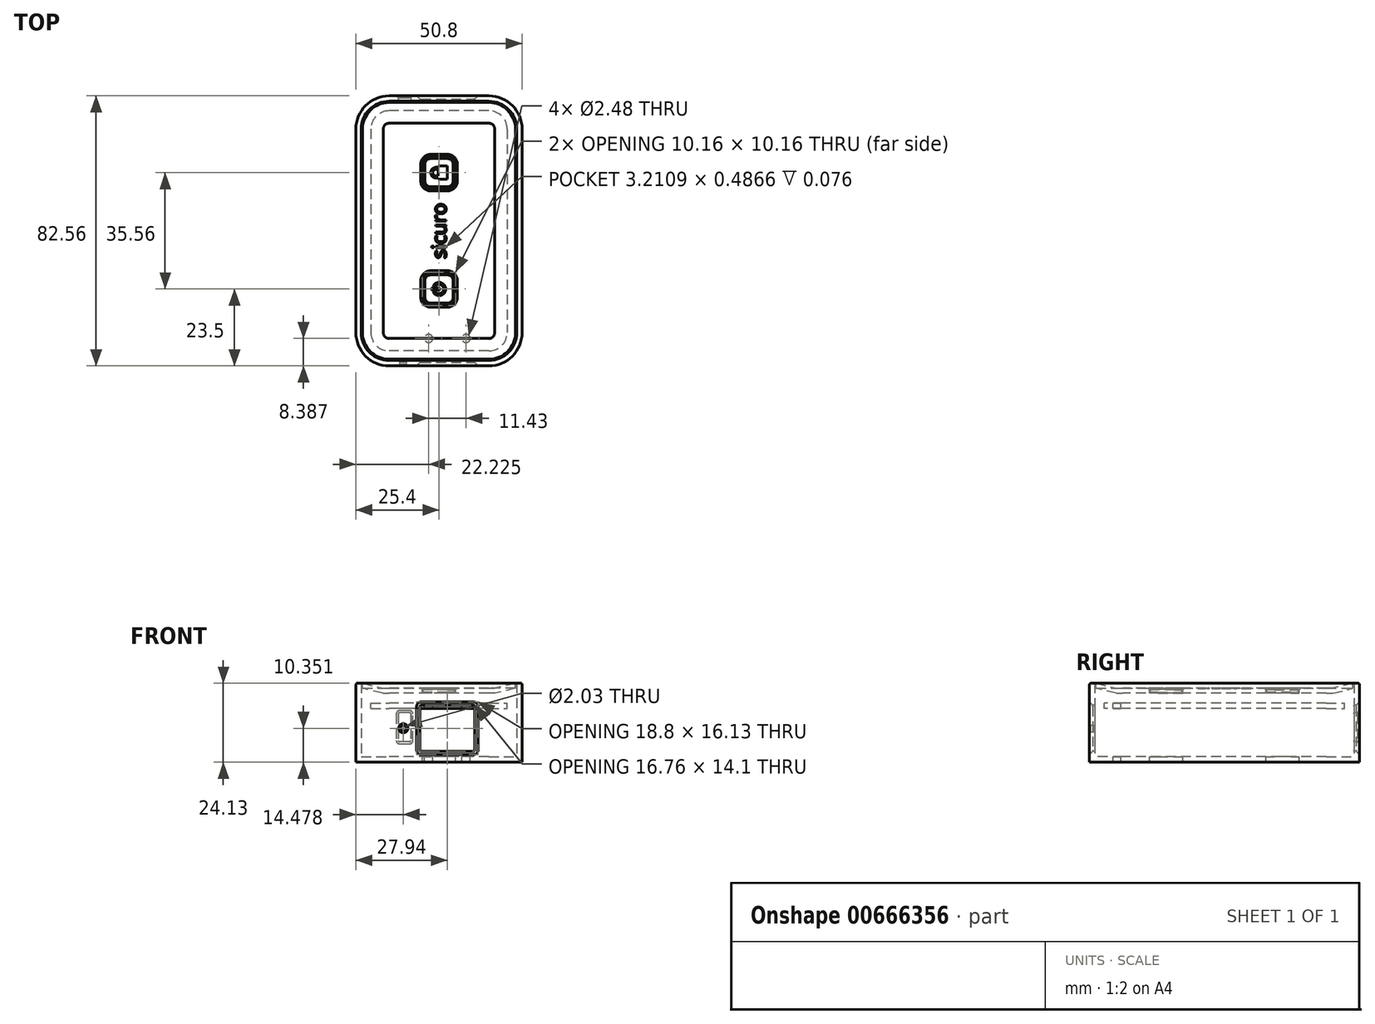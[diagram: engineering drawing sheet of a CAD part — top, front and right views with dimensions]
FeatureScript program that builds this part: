
annotation { "Feature Type Name" : "Feature", "Feature Type Description" : "" }
export const myFeature = defineFeature(function(context is Context, id is Id, definition is map)
    precondition{}
    {
        {
            var Q0;
            Q0=qCreatedBy(makeId("Top.planeOp"),FACE);
            var sketch = newSketch(context, id + "F0", { "sketchPlane" : qUnion([Q0])});
            skLineSegment(sketch, "E0.bottom", {"start": v(25.4, 41.28) * mm, "end": v(-25.4, 41.28) * mm});
            skLineSegment(sketch, "E0.top", {"start": v(25.4, -41.28) * mm, "end": v(-25.4, -41.28) * mm});
            skLineSegment(sketch, "E0.left", {"start": v(25.4, 41.28) * mm, "end": v(25.4, -41.28) * mm});
            skLineSegment(sketch, "E0.right", {"start": v(-25.4, 41.28) * mm, "end": v(-25.4, -41.28) * mm});
            skPoint(sketch, "E0.middle", {"position": v(0, 0) * mm});
            skSolve(sketch);
        }
        {
            var Q0;
            Q0 = qSketchRegion(id + "F0", true);
            extrude(context, id + "F1", {"entities" : qUnion([Q0]), "depth" : 24.13 * mm, "offsetDistance" : 25.4 * mm});
        }
        {
            var Q0;
            Q0=makeQuery(id+"F1.opExtrude","SWEPT_EDGE",EDGE,{"disambiguationData":[OSD([sQuery(id+"F0.wireOp",EDGE,"E0.top"),sQuery(id+"F0.wireOp",EDGE,"E0.left")])]});
            var Q1;
            Q1=makeQuery(id+"F1.opExtrude","SWEPT_EDGE",EDGE,{"disambiguationData":[OSD([sQuery(id+"F0.wireOp",EDGE,"E0.top"),sQuery(id+"F0.wireOp",EDGE,"E0.right")])]});
            var Q2;
            Q2=makeQuery(id+"F1.opExtrude","SWEPT_EDGE",EDGE,{"disambiguationData":[OSD([sQuery(id+"F0.wireOp",EDGE,"E0.bottom"),sQuery(id+"F0.wireOp",EDGE,"E0.left")])]});
            var Q3;
            Q3=makeQuery(id+"F1.opExtrude","SWEPT_EDGE",EDGE,{"disambiguationData":[OSD([sQuery(id+"F0.wireOp",EDGE,"E0.bottom"),sQuery(id+"F0.wireOp",EDGE,"E0.right")])]});
            fillet(context, id + "F2", {"entities" : qUnion([Q0, Q1, Q2, Q3]), "radius" : 10.16 * mm, "tangentPropagation" : true, "allowEdgeOverflow" : false});
        }
        {
            var Q0;
            Q0=makeQuery(id+"F1.opExtrude","CAP_FACE",FACE,{"disambiguationData":[OSD([sQuery(id+"F0.wireOp",EDGE,"E0.bottom"),sQuery(id+"F0.wireOp",EDGE,"E0.top"),sQuery(id+"F0.wireOp",EDGE,"E0.left"),sQuery(id+"F0.wireOp",EDGE,"E0.right")])],"isStart":false});
            shell(context, id + "F3", {"entities" : qUnion([Q0]), "thickness" : 1.65 * mm});
        }
        {
            var Q0;
            Q0=makeQuery(id+"F1.opExtrude","CAP_EDGE",EDGE,{"disambiguationData":[OSD([sQuery(id+"F0.wireOp",EDGE,"E0.right")])],"isStart":false});
            var Q1;
            {var subQ0=sQuery(id+"F0.wireOp",EDGE,"E0.right");var subQ1=sQuery(id+"F0.wireOp",EDGE,"E0.bottom");Q1=makeQuery(id+"F2.opFillet","BLEND_EDGE",EDGE,{"blendedFrom":[makeQuery(id+"F1.opExtrude","SWEPT_EDGE",EDGE,{"disambiguationData":[OSD([subQ1,subQ0])]}),makeQuery(id+"F1.opExtrude","CAP_FACE",FACE,{"disambiguationData":[OSD([subQ1,sQuery(id+"F0.wireOp",EDGE,"E0.top"),sQuery(id+"F0.wireOp",EDGE,"E0.left"),subQ0])],"isStart":false})],"blendedInto":[makeQuery(id+"F1.opExtrude","CAP_FACE",FACE,{"disambiguationData":[OSD([subQ1,sQuery(id+"F0.wireOp",EDGE,"E0.top"),sQuery(id+"F0.wireOp",EDGE,"E0.left"),subQ0])],"isStart":false})]});}
            var Q2;
            Q2=makeQuery(id+"F1.opExtrude","CAP_EDGE",EDGE,{"disambiguationData":[OSD([sQuery(id+"F0.wireOp",EDGE,"E0.bottom")])],"isStart":false});
            var Q3;
            {var subQ0=sQuery(id+"F0.wireOp",EDGE,"E0.left");var subQ1=sQuery(id+"F0.wireOp",EDGE,"E0.bottom");Q3=makeQuery(id+"F2.opFillet","BLEND_EDGE",EDGE,{"blendedFrom":[makeQuery(id+"F1.opExtrude","SWEPT_EDGE",EDGE,{"disambiguationData":[OSD([subQ1,subQ0])]}),makeQuery(id+"F1.opExtrude","CAP_FACE",FACE,{"disambiguationData":[OSD([subQ1,sQuery(id+"F0.wireOp",EDGE,"E0.top"),subQ0,sQuery(id+"F0.wireOp",EDGE,"E0.right")])],"isStart":false})],"blendedInto":[makeQuery(id+"F1.opExtrude","CAP_FACE",FACE,{"disambiguationData":[OSD([subQ1,sQuery(id+"F0.wireOp",EDGE,"E0.top"),subQ0,sQuery(id+"F0.wireOp",EDGE,"E0.right")])],"isStart":false})]});}
            var Q4;
            Q4=makeQuery(id+"F1.opExtrude","CAP_EDGE",EDGE,{"disambiguationData":[OSD([sQuery(id+"F0.wireOp",EDGE,"E0.left")])],"isStart":false});
            var Q5;
            {var subQ0=sQuery(id+"F0.wireOp",EDGE,"E0.left");var subQ1=sQuery(id+"F0.wireOp",EDGE,"E0.top");Q5=makeQuery(id+"F2.opFillet","BLEND_EDGE",EDGE,{"blendedFrom":[makeQuery(id+"F1.opExtrude","SWEPT_EDGE",EDGE,{"disambiguationData":[OSD([subQ1,subQ0])]}),makeQuery(id+"F1.opExtrude","CAP_FACE",FACE,{"disambiguationData":[OSD([sQuery(id+"F0.wireOp",EDGE,"E0.bottom"),subQ1,subQ0,sQuery(id+"F0.wireOp",EDGE,"E0.right")])],"isStart":false})],"blendedInto":[makeQuery(id+"F1.opExtrude","CAP_FACE",FACE,{"disambiguationData":[OSD([sQuery(id+"F0.wireOp",EDGE,"E0.bottom"),subQ1,subQ0,sQuery(id+"F0.wireOp",EDGE,"E0.right")])],"isStart":false})]});}
            var Q6;
            {var subQ0=sQuery(id+"F0.wireOp",EDGE,"E0.right");var subQ1=sQuery(id+"F0.wireOp",EDGE,"E0.top");Q6=makeQuery(id+"F2.opFillet","BLEND_EDGE",EDGE,{"blendedFrom":[makeQuery(id+"F1.opExtrude","SWEPT_EDGE",EDGE,{"disambiguationData":[OSD([subQ1,subQ0])]}),makeQuery(id+"F1.opExtrude","CAP_FACE",FACE,{"disambiguationData":[OSD([sQuery(id+"F0.wireOp",EDGE,"E0.bottom"),subQ1,sQuery(id+"F0.wireOp",EDGE,"E0.left"),subQ0])],"isStart":false})],"blendedInto":[makeQuery(id+"F1.opExtrude","CAP_FACE",FACE,{"disambiguationData":[OSD([sQuery(id+"F0.wireOp",EDGE,"E0.bottom"),subQ1,sQuery(id+"F0.wireOp",EDGE,"E0.left"),subQ0])],"isStart":false})]});}
            var Q7;
            Q7=makeQuery(id+"F1.opExtrude","CAP_EDGE",EDGE,{"disambiguationData":[OSD([sQuery(id+"F0.wireOp",EDGE,"E0.top")])],"isStart":false});
            fillet(context, id + "F4", {"entities" : qUnion([Q0, Q1, Q2, Q3, Q4, Q5, Q6, Q7]), "radius" : 0.5 * mm, "tangentPropagation" : true, "allowEdgeOverflow" : false});
        }
        {
            var Q0;
            Q0=makeQuery(id+"F1.opExtrude","CAP_FACE",FACE,{"disambiguationData":[OSD([sQuery(id+"F0.wireOp",EDGE,"E0.bottom"),sQuery(id+"F0.wireOp",EDGE,"E0.top"),sQuery(id+"F0.wireOp",EDGE,"E0.left"),sQuery(id+"F0.wireOp",EDGE,"E0.right")])],"isStart":false});
            var sketch = newSketch(context, id + "F5", { "sketchPlane" : qUnion([Q0])});
            skArc(sketch, "E1.0", {"start": v(-15.24, 39.24) * mm, "mid": v(-20.99, 36.86) * mm, "end": v(-23.37, 31.12) * mm});
            skLineSegment(sketch, "E1.1", {"start": v(15.24, 39.24) * mm, "end": v(-15.24, 39.24) * mm});
            skLineSegment(sketch, "E1.2", {"start": v(-23.37, 31.12) * mm, "end": v(-23.37, -31.12) * mm});
            skArc(sketch, "E1.3", {"start": v(23.37, 31.12) * mm, "mid": v(20.99, 36.86) * mm, "end": v(15.24, 39.24) * mm});
            skArc(sketch, "E1.4", {"start": v(-23.37, -31.12) * mm, "mid": v(-20.99, -36.86) * mm, "end": v(-15.24, -39.24) * mm});
            skLineSegment(sketch, "E1.5", {"start": v(15.24, -39.24) * mm, "end": v(-15.24, -39.24) * mm});
            skArc(sketch, "E1.6", {"start": v(15.24, -39.24) * mm, "mid": v(20.99, -36.86) * mm, "end": v(23.37, -31.12) * mm});
            skLineSegment(sketch, "E1.7", {"start": v(23.37, 31.12) * mm, "end": v(23.37, -31.12) * mm});
            skSolve(sketch);
        }
        {
            var Q0;
            Q0 = qSketchRegion(id + "F5", true);
            extrude(context, id + "F6", {"entities" : qUnion([Q0]), "oppositeDirection" : true, "depth" : 6.35 * mm, "offsetDistance" : 25.4 * mm});
        }
        {
            var Q0;
            Q0=makeQuery(id+"F6.opExtrude","CAP_FACE",FACE,{"disambiguationData":[OSD([sQuery(id+"F5.wireOp",EDGE,"E1.0"),sQuery(id+"F5.wireOp",EDGE,"E1.1"),sQuery(id+"F5.wireOp",EDGE,"E1.2"),sQuery(id+"F5.wireOp",EDGE,"E1.3"),sQuery(id+"F5.wireOp",EDGE,"E1.4"),sQuery(id+"F5.wireOp",EDGE,"E1.5"),sQuery(id+"F5.wireOp",EDGE,"E1.6"),sQuery(id+"F5.wireOp",EDGE,"E1.7")])],"isStart":true});
            var sketch = newSketch(context, id + "F7", { "sketchPlane" : qUnion([Q0])});
            skLineSegment(sketch, "E2.0", {"start": v(15.24, 32.9) * mm, "end": v(-15.24, 32.9) * mm});
            skArc(sketch, "E2.1", {"start": v(17.02, 31.12) * mm, "mid": v(16.5, 32.37) * mm, "end": v(15.24, 32.9) * mm});
            skArc(sketch, "E2.2", {"start": v(-15.24, 32.9) * mm, "mid": v(-16.5, 32.37) * mm, "end": v(-17.02, 31.12) * mm});
            skLineSegment(sketch, "E2.3", {"start": v(17.02, 31.12) * mm, "end": v(17.02, -31.12) * mm});
            skLineSegment(sketch, "E2.4", {"start": v(-17.02, 31.12) * mm, "end": v(-17.02, -31.12) * mm});
            skArc(sketch, "E2.5", {"start": v(-17.02, -31.12) * mm, "mid": v(-16.5, -32.37) * mm, "end": v(-15.24, -32.9) * mm});
            skLineSegment(sketch, "E2.6", {"start": v(15.24, -32.9) * mm, "end": v(-15.24, -32.9) * mm});
            skArc(sketch, "E2.7", {"start": v(15.24, -32.9) * mm, "mid": v(16.5, -32.37) * mm, "end": v(17.02, -31.12) * mm});
            skSolve(sketch);
        }
        {
            var Q0;
            Q0=sQuery(id+"F7.wireOp",VERTEX,"E2.7.start");
            var Q1;
            Q1=qCreatedBy(makeId("Right.planeOp"),FACE);
            cPlane(context, id + "F8", {"entities" : qUnion([Q0, Q1]), "cplaneType" : CPlaneType.PLANE_POINT, "offset" : 25.4 * mm, "width" : 152.4 * mm, "height" : 152.4 * mm});
        }
        {
            var Q0;
            Q0=qCreatedBy(id+"F8.planeOp",FACE);
            var sketch = newSketch(context, id + "F9", { "sketchPlane" : qUnion([Q0])});
            skPoint(sketch, "E3.0", {"position": v(-32.9, 24.13) * mm});
            skPoint(sketch, "E4.0", {"position": v(-39.24, 24.13) * mm});
            skLineSegment(sketch, "E5", {"start": v(-39.24, 24.13) * mm, "end": v(-32.9, 22.6) * mm});
            skLineSegment(sketch, "E6", {"start": v(-32.9, 22.6) * mm, "end": v(-32.9, 26.9) * mm});
            skLineSegment(sketch, "E7", {"start": v(-39.24, 24.13) * mm, "end": v(-39.2, 26.9) * mm});
            skLineSegment(sketch, "E8", {"start": v(-39.2, 26.9) * mm, "end": v(-32.9, 26.9) * mm});
            skSolve(sketch);
        }
        {
            var Q0;
            Q0 = qSketchRegion(id + "F9", true);
            var Q1;
            Q1 = qBodyType(qCreatedBy(id + "F7" ,EDGE), BodyType.WIRE);
            sweep(context, id + "F10", {"operationType" : NewBodyOperationType.REMOVE, "profiles" : qUnion([Q0]), "path" : qUnion([Q1])});
        }
        {
            var Q0;
            Q0 = qSketchRegion(id + "F7", true);
            extrude(context, id + "F11", {"entities" : qUnion([Q0]), "operationType" : NewBodyOperationType.REMOVE, "oppositeDirection" : true, "depth" : 1.52 * mm, "offsetDistance" : 25.4 * mm});
        }
        {
            var Q0;
            Q0=qCreatedBy(makeId("Front.planeOp"),FACE);
            var sketch = newSketch(context, id + "F12", { "sketchPlane" : qUnion([Q0])});
            skLineSegment(sketch, "E9.bottom", {"start": v(10.16, 16.64) * mm, "end": v(-5.08, 16.64) * mm, "construction": true});
            skLineSegment(sketch, "E9.top", {"start": v(10.16, 4.06) * mm, "end": v(-5.08, 4.06) * mm, "construction": true});
            skLineSegment(sketch, "E9.left", {"start": v(10.16, 16.64) * mm, "end": v(10.16, 4.06) * mm, "construction": true});
            skLineSegment(sketch, "E9.right", {"start": v(-5.08, 16.64) * mm, "end": v(-5.08, 4.06) * mm, "construction": true});
            skPoint(sketch, "E9.middle", {"position": v(2.54, 10.35) * mm});
            skLineSegment(sketch, "E10.0", {"start": v(10.92, 17.4) * mm, "end": v(-5.84, 17.4) * mm});
            skLineSegment(sketch, "E10.1", {"start": v(10.92, 17.4) * mm, "end": v(10.92, 3.3) * mm});
            skLineSegment(sketch, "E10.2", {"start": v(10.92, 3.3) * mm, "end": v(-5.84, 3.3) * mm});
            skLineSegment(sketch, "E10.3", {"start": v(-5.84, 17.4) * mm, "end": v(-5.84, 3.3) * mm});
            skSolve(sketch);
        }
        {
            var Q0;
            Q0 = qSketchRegion(id + "F12", true);
            extrude(context, id + "F13", {"entities" : qUnion([Q0]), "operationType" : NewBodyOperationType.REMOVE, "endBound" : BoundingType.THROUGH_ALL, "oppositeDirection" : true, "depth" : 25.4 * mm, "offsetDistance" : 25.4 * mm, "hasSecondDirection" : true, "secondDirectionBound" : SecondDirectionBoundingType.THROUGH_ALL, "secondDirectionOppositeDirection" : false, "secondDirectionDepth" : 25.4 * mm});
        }
        {
            var Q0;
            Q0=makeQuery(id+"F6.opExtrude","CAP_FACE",FACE,{"disambiguationData":[OSD([sQuery(id+"F5.wireOp",EDGE,"E1.0"),sQuery(id+"F5.wireOp",EDGE,"E1.1"),sQuery(id+"F5.wireOp",EDGE,"E1.2"),sQuery(id+"F5.wireOp",EDGE,"E1.3"),sQuery(id+"F5.wireOp",EDGE,"E1.4"),sQuery(id+"F5.wireOp",EDGE,"E1.5"),sQuery(id+"F5.wireOp",EDGE,"E1.6"),sQuery(id+"F5.wireOp",EDGE,"E1.7")])],"isStart":false});
            var Q1;
            Q1=makeQuery(id+"F6.opExtrude","SWEPT_FACE",FACE,{"disambiguationData":[OSD([sQuery(id+"F5.wireOp",EDGE,"E1.5")])]});
            var Q2;
            Q2=makeQuery(id+"F6.opExtrude","SWEPT_FACE",FACE,{"disambiguationData":[OSD([sQuery(id+"F5.wireOp",EDGE,"E1.6")])]});
            var Q3;
            Q3=makeQuery(id+"F6.opExtrude","SWEPT_FACE",FACE,{"disambiguationData":[OSD([sQuery(id+"F5.wireOp",EDGE,"E1.4")])]});
            var Q4;
            Q4=makeQuery(id+"F6.opExtrude","SWEPT_FACE",FACE,{"disambiguationData":[OSD([sQuery(id+"F5.wireOp",EDGE,"E1.7")])]});
            var Q5;
            Q5=makeQuery(id+"F6.opExtrude","SWEPT_FACE",FACE,{"disambiguationData":[OSD([sQuery(id+"F5.wireOp",EDGE,"E1.3")])]});
            var Q6;
            Q6=makeQuery(id+"F6.opExtrude","SWEPT_FACE",FACE,{"disambiguationData":[OSD([sQuery(id+"F5.wireOp",EDGE,"E1.1")])]});
            var Q7;
            Q7=makeQuery(id+"F6.opExtrude","SWEPT_FACE",FACE,{"disambiguationData":[OSD([sQuery(id+"F5.wireOp",EDGE,"E1.0")])]});
            var Q8;
            Q8=makeQuery(id+"F6.opExtrude","SWEPT_FACE",FACE,{"disambiguationData":[OSD([sQuery(id+"F5.wireOp",EDGE,"E1.2")])]});
            shell(context, id + "F14", {"entities" : qUnion([Q0, Q1, Q2, Q3, Q4, Q5, Q6, Q7, Q8]), "thickness" : 1.52 * mm});
        }
        {
            var Q0;
            Q0=makeQuery(id+"F5.imprint","IMPRINT",FACE,{"disambiguationData":[TD([[makeQuery(id+"F5.imprint","IMPRINT",EDGE,{"derivedFrom":sQuery(id+"F5.wireOp",EDGE,"E1.0")}),1.0]])]});
            var sketch = newSketch(context, id + "F15", { "sketchPlane" : qUnion([Q0])});
            skLineSegment(sketch, "E11.bottom", {"start": v(2.54, 22.86) * mm, "end": v(-2.54, 22.86) * mm});
            skLineSegment(sketch, "E11.top", {"start": v(2.54, 12.7) * mm, "end": v(-2.54, 12.7) * mm});
            skLineSegment(sketch, "E11.left", {"start": v(5.08, 20.32) * mm, "end": v(5.08, 15.24) * mm});
            skLineSegment(sketch, "E11.right", {"start": v(-5.08, 20.32) * mm, "end": v(-5.08, 15.24) * mm});
            skPoint(sketch, "E11.middle", {"position": v(0, 17.78) * mm});
            skPoint(sketch, "E12.visualSharp", {"position": v(-5.08, 22.86) * mm});
            skArc(sketch, "E12.filletArc", {"start": v(-2.54, 22.86) * mm, "mid": v(-4.34, 22.12) * mm, "end": v(-5.08, 20.32) * mm});
            skPoint(sketch, "E13.visualSharp", {"position": v(5.08, 22.86) * mm});
            skArc(sketch, "E13.filletArc", {"start": v(5.08, 20.32) * mm, "mid": v(4.34, 22.12) * mm, "end": v(2.54, 22.86) * mm});
            skPoint(sketch, "E14.visualSharp", {"position": v(5.08, 12.7) * mm});
            skArc(sketch, "E14.filletArc", {"start": v(2.54, 12.7) * mm, "mid": v(4.34, 13.44) * mm, "end": v(5.08, 15.24) * mm});
            skPoint(sketch, "E15.visualSharp", {"position": v(-5.08, 12.7) * mm});
            skArc(sketch, "E15.filletArc", {"start": v(-5.08, 15.24) * mm, "mid": v(-4.34, 13.44) * mm, "end": v(-2.54, 12.7) * mm});
            skArc(sketch, "E16.MirrorCS", {"start": v(-2.54, -22.86) * mm, "mid": v(-4.34, -22.12) * mm, "end": v(-5.08, -20.32) * mm});
            skLineSegment(sketch, "E17.MirrorCS", {"start": v(-5.08, -20.32) * mm, "end": v(-5.08, -15.24) * mm});
            skLineSegment(sketch, "E18.MirrorCS", {"start": v(5.08, -20.32) * mm, "end": v(5.08, -15.24) * mm});
            skArc(sketch, "E19.MirrorCS", {"start": v(2.54, -12.7) * mm, "mid": v(4.34, -13.44) * mm, "end": v(5.08, -15.24) * mm});
            skArc(sketch, "E20.MirrorCS", {"start": v(-5.08, -15.24) * mm, "mid": v(-4.34, -13.44) * mm, "end": v(-2.54, -12.7) * mm});
            skLineSegment(sketch, "E21.MirrorCS", {"start": v(2.54, -12.7) * mm, "end": v(-2.54, -12.7) * mm});
            skArc(sketch, "E22.MirrorCS", {"start": v(5.08, -20.32) * mm, "mid": v(4.34, -22.12) * mm, "end": v(2.54, -22.86) * mm});
            skLineSegment(sketch, "E23.MirrorCS", {"start": v(2.54, -22.86) * mm, "end": v(-2.54, -22.86) * mm});
            skSolve(sketch);
        }
        {
            var Q0;
            Q0 = qSketchRegion(id + "F15", true);
            extrude(context, id + "F16", {"entities" : qUnion([Q0]), "operationType" : NewBodyOperationType.REMOVE, "endBound" : BoundingType.THROUGH_ALL, "oppositeDirection" : true, "depth" : 25.4 * mm, "offsetDistance" : 25.4 * mm});
        }
        {
            var Q0;
            Q0=makeQuery(id+"F16.boolean.opBoolean","INTERSECT",EDGE,{"derivedFrom":[makeQuery(id+"F11.boolean.opBoolean","COPY",FACE,{"derivedFrom":makeQuery(id+"F11.opExtrude","CAP_FACE",FACE,{"disambiguationData":[OSD([sQuery(id+"F7.wireOp",EDGE,"E2.0"),sQuery(id+"F7.wireOp",EDGE,"E2.1"),sQuery(id+"F7.wireOp",EDGE,"E2.2"),sQuery(id+"F7.wireOp",EDGE,"E2.3"),sQuery(id+"F7.wireOp",EDGE,"E2.4"),sQuery(id+"F7.wireOp",EDGE,"E2.5"),sQuery(id+"F7.wireOp",EDGE,"E2.6"),sQuery(id+"F7.wireOp",EDGE,"E2.7")])],"isStart":false})}),makeQuery(id+"F16.opExtrude","SWEPT_FACE",FACE,{"disambiguationData":[OSD([sQuery(id+"F15.wireOp",EDGE,"E18.MirrorCS")])]})]});
            var Q1;
            Q1=makeQuery(id+"F16.boolean.opBoolean","INTERSECT",EDGE,{"derivedFrom":[makeQuery(id+"F11.boolean.opBoolean","COPY",FACE,{"derivedFrom":makeQuery(id+"F11.opExtrude","CAP_FACE",FACE,{"disambiguationData":[OSD([sQuery(id+"F7.wireOp",EDGE,"E2.0"),sQuery(id+"F7.wireOp",EDGE,"E2.1"),sQuery(id+"F7.wireOp",EDGE,"E2.2"),sQuery(id+"F7.wireOp",EDGE,"E2.3"),sQuery(id+"F7.wireOp",EDGE,"E2.4"),sQuery(id+"F7.wireOp",EDGE,"E2.5"),sQuery(id+"F7.wireOp",EDGE,"E2.6"),sQuery(id+"F7.wireOp",EDGE,"E2.7")])],"isStart":false})}),makeQuery(id+"F16.opExtrude","SWEPT_FACE",FACE,{"disambiguationData":[OSD([sQuery(id+"F15.wireOp",EDGE,"E11.left")])]})]});
            chamfer(context, id + "F17", {"entities" : qUnion([Q0, Q1]), "width" : 0.5 * mm, "tangentPropagation" : true});
        }
        {
            var Q0;
            {var subQ0=makeQuery(id+"F11.boolean.opBoolean","COPY",FACE,{"derivedFrom":makeQuery(id+"F11.opExtrude","CAP_FACE",FACE,{"disambiguationData":[OSD([sQuery(id+"F7.wireOp",EDGE,"E2.0"),sQuery(id+"F7.wireOp",EDGE,"E2.1"),sQuery(id+"F7.wireOp",EDGE,"E2.2"),sQuery(id+"F7.wireOp",EDGE,"E2.3"),sQuery(id+"F7.wireOp",EDGE,"E2.4"),sQuery(id+"F7.wireOp",EDGE,"E2.5"),sQuery(id+"F7.wireOp",EDGE,"E2.6"),sQuery(id+"F7.wireOp",EDGE,"E2.7")])],"isStart":false})});Q0=makeQuery(id+"F17.opChamfer","BLEND_VERTEX",VERTEX,{"blendedFrom":[makeQuery(id+"F16.boolean.opBoolean","INTERSECT",EDGE,{"derivedFrom":[subQ0,makeQuery(id+"F16.opExtrude","SWEPT_FACE",FACE,{"disambiguationData":[OSD([sQuery(id+"F15.wireOp",EDGE,"E11.top")])]})]}),makeQuery(id+"F16.boolean.opBoolean","INTERSECT",EDGE,{"derivedFrom":[subQ0,makeQuery(id+"F16.opExtrude","SWEPT_FACE",FACE,{"disambiguationData":[OSD([sQuery(id+"F15.wireOp",EDGE,"E15.filletArc")])]})]}),subQ0],"blendedInto":[subQ0]});}
            var Q1;
            Q1=qCreatedBy(makeId("Top.planeOp"),FACE);
            cPlane(context, id + "F18", {"entities" : qUnion([Q0, Q1]), "cplaneType" : CPlaneType.PLANE_POINT, "offset" : 25.4 * mm, "width" : 152.4 * mm, "height" : 152.4 * mm});
        }
        {
            var Q0;
            Q0=qCreatedBy(id+"F18.planeOp",FACE);
            var sketch = newSketch(context, id + "F19", { "sketchPlane" : qUnion([Q0])});
            skArc(sketch, "E24.0", {"start": v(2.54, -12.95) * mm, "mid": v(4.16, -13.62) * mm, "end": v(4.83, -15.24) * mm});
            skLineSegment(sketch, "E24.1", {"start": v(4.83, -20.32) * mm, "end": v(4.83, -15.24) * mm});
            skLineSegment(sketch, "E24.2", {"start": v(2.54, -12.95) * mm, "end": v(-2.54, -12.95) * mm});
            skArc(sketch, "E24.3", {"start": v(4.83, -20.32) * mm, "mid": v(4.16, -21.94) * mm, "end": v(2.54, -22.6) * mm});
            skArc(sketch, "E24.4", {"start": v(-4.83, -15.24) * mm, "mid": v(-4.16, -13.62) * mm, "end": v(-2.54, -12.95) * mm});
            skLineSegment(sketch, "E24.5", {"start": v(-4.83, -20.32) * mm, "end": v(-4.83, -15.24) * mm});
            skArc(sketch, "E24.6", {"start": v(-2.54, -22.6) * mm, "mid": v(-4.16, -21.94) * mm, "end": v(-4.83, -20.32) * mm});
            skLineSegment(sketch, "E24.7", {"start": v(2.54, -22.6) * mm, "end": v(-2.54, -22.6) * mm});
            skArc(sketch, "E25.0", {"start": v(4.83, 20.32) * mm, "mid": v(4.16, 21.94) * mm, "end": v(2.54, 22.6) * mm});
            skLineSegment(sketch, "E25.1", {"start": v(4.83, 20.32) * mm, "end": v(4.83, 15.24) * mm});
            skLineSegment(sketch, "E25.2", {"start": v(2.54, 22.6) * mm, "end": v(-2.54, 22.6) * mm});
            skArc(sketch, "E25.3", {"start": v(2.54, 12.95) * mm, "mid": v(4.16, 13.62) * mm, "end": v(4.83, 15.24) * mm});
            skArc(sketch, "E25.4", {"start": v(-2.54, 22.6) * mm, "mid": v(-4.16, 21.94) * mm, "end": v(-4.83, 20.32) * mm});
            skLineSegment(sketch, "E25.5", {"start": v(-4.83, 20.32) * mm, "end": v(-4.83, 15.24) * mm});
            skArc(sketch, "E25.6", {"start": v(-4.83, 15.24) * mm, "mid": v(-4.16, 13.62) * mm, "end": v(-2.54, 12.95) * mm});
            skLineSegment(sketch, "E25.7", {"start": v(2.54, 12.95) * mm, "end": v(-2.54, 12.95) * mm});
            skSolve(sketch);
        }
        {
            var Q0;
            Q0 = qSketchRegion(id + "F19", true);
            extrude(context, id + "F20", {"entities" : qUnion([Q0]), "oppositeDirection" : true, "depth" : 1.27 * mm, "offsetDistance" : 25.4 * mm});
        }
        {
            var Q0;
            Q0=makeQuery(id+"F14.opShell","OFFSET_FACE",FACE,{"disambiguationData":[OSD([sQuery(id+"F7.wireOp",EDGE,"E2.0"),sQuery(id+"F7.wireOp",EDGE,"E2.1"),sQuery(id+"F7.wireOp",EDGE,"E2.2"),sQuery(id+"F7.wireOp",EDGE,"E2.3"),sQuery(id+"F7.wireOp",EDGE,"E2.4"),sQuery(id+"F7.wireOp",EDGE,"E2.5"),sQuery(id+"F7.wireOp",EDGE,"E2.6"),sQuery(id+"F7.wireOp",EDGE,"E2.7")])]});
            cPlane(context, id + "F21", {"entities" : qUnion([Q0]), "cplaneType" : CPlaneType.OFFSET, "offset" : 3.05 * mm, "width" : 152.4 * mm, "height" : 152.4 * mm});
        }
        {
            var Q0;
            Q0=qCreatedBy(id+"F21.planeOp",FACE);
            var sketch = newSketch(context, id + "F22", { "sketchPlane" : qUnion([Q0])});
            skLineSegment(sketch, "E26.0", {"start": v(-20.83, -31.12) * mm, "end": v(-20.83, 31.12) * mm});
            skArc(sketch, "E26.1", {"start": v(-15.24, -36.7) * mm, "mid": v(-19.2, -35.07) * mm, "end": v(-20.83, -31.12) * mm});
            skArc(sketch, "E26.2", {"start": v(-20.83, 31.12) * mm, "mid": v(-19.2, 35.07) * mm, "end": v(-15.24, 36.7) * mm});
            skLineSegment(sketch, "E26.3", {"start": v(15.24, -36.7) * mm, "end": v(-15.24, -36.7) * mm});
            skLineSegment(sketch, "E26.4", {"start": v(15.24, 36.7) * mm, "end": v(-15.24, 36.7) * mm});
            skArc(sketch, "E26.5", {"start": v(15.24, 36.7) * mm, "mid": v(19.2, 35.07) * mm, "end": v(20.83, 31.12) * mm});
            skLineSegment(sketch, "E26.6", {"start": v(20.83, -31.12) * mm, "end": v(20.83, 31.12) * mm});
            skArc(sketch, "E26.7", {"start": v(20.83, -31.12) * mm, "mid": v(19.2, -35.07) * mm, "end": v(15.24, -36.7) * mm});
            skSolve(sketch);
        }
        {
            var Q0;
            Q0 = qSketchRegion(id + "F22", true);
            extrude(context, id + "F23", {"entities" : qUnion([Q0]), "depth" : 1.65 * mm, "offsetDistance" : 25.4 * mm});
        }
        {
            var Q0;
            Q0=qCreatedBy(id+"F21.planeOp",FACE);
            var sketch = newSketch(context, id + "F24", { "sketchPlane" : qUnion([Q0])});
            skLineSegment(sketch, "E27.0", {"start": v(15.24, 36.7) * mm, "end": v(-15.24, 36.7) * mm, "construction": true});
            skArc(sketch, "E28.0.0", {"start": v(15.24, -36.7) * mm, "mid": v(19.2, -35.07) * mm, "end": v(20.83, -31.12) * mm, "construction": true});
            skLineSegment(sketch, "E28.0.1", {"start": v(20.83, -31.12) * mm, "end": v(20.83, 31.12) * mm, "construction": true});
            skArc(sketch, "E28.0.2", {"start": v(20.83, 31.12) * mm, "mid": v(19.2, 35.07) * mm, "end": v(15.24, 36.7) * mm, "construction": true});
            skArc(sketch, "E28.0.4", {"start": v(-15.24, 36.7) * mm, "mid": v(-19.2, 35.07) * mm, "end": v(-20.83, 31.12) * mm, "construction": true});
            skLineSegment(sketch, "E28.0.5", {"start": v(-20.83, 31.12) * mm, "end": v(-20.83, -31.12) * mm, "construction": true});
            skArc(sketch, "E28.0.6", {"start": v(-20.83, -31.12) * mm, "mid": v(-19.2, -35.07) * mm, "end": v(-15.24, -36.7) * mm, "construction": true});
            skLineSegment(sketch, "E28.0.7", {"start": v(-15.24, -36.7) * mm, "end": v(15.24, -36.7) * mm, "construction": true});
            skLineSegment(sketch, "E29.0.0", {"start": v(15.24, -40.77) * mm, "end": v(-15.24, -40.77) * mm, "construction": true});
            skArc(sketch, "E29.0.1", {"start": v(-15.24, -40.77) * mm, "mid": v(-22.06, -37.94) * mm, "end": v(-24.9, -31.12) * mm, "construction": true});
            skLineSegment(sketch, "E29.0.2", {"start": v(-24.9, -31.12) * mm, "end": v(-24.9, 31.12) * mm, "construction": true});
            skArc(sketch, "E29.0.3", {"start": v(-24.9, 31.12) * mm, "mid": v(-22.06, 37.94) * mm, "end": v(-15.24, 40.77) * mm, "construction": true});
            skLineSegment(sketch, "E29.0.4", {"start": v(-15.24, 40.77) * mm, "end": v(15.24, 40.77) * mm, "construction": true});
            skArc(sketch, "E29.0.5", {"start": v(15.24, 40.77) * mm, "mid": v(22.06, 37.94) * mm, "end": v(24.9, 31.12) * mm, "construction": true});
            skLineSegment(sketch, "E29.0.6", {"start": v(24.9, 31.12) * mm, "end": v(24.9, -31.12) * mm, "construction": true});
            skArc(sketch, "E29.0.7", {"start": v(24.9, -31.12) * mm, "mid": v(22.06, -37.94) * mm, "end": v(15.24, -40.77) * mm, "construction": true});
            skPoint(sketch, "E30.0", {"position": v(0, 0) * mm});
            skLineSegment(sketch, "E31", {"start": v(2.54, 0) * mm, "end": v(2.54, 42.72) * mm, "construction": true});
            skCircle(sketch, "E32", {"center": v(-3.18, 32.9) * mm, "radius": 1.24 * mm});
            skCircle(sketch, "E33", {"center": v(8.25, 32.9) * mm, "radius": 1.24 * mm});
            skSolve(sketch);
        }
        {
            var Q0;
            Q0 = qSketchRegion(id + "F24", true);
            extrude(context, id + "F25", {"entities" : qUnion([Q0]), "operationType" : NewBodyOperationType.REMOVE, "endBound" : BoundingType.THROUGH_ALL, "depth" : 25.4 * mm, "offsetDistance" : 25.4 * mm});
        }
        {
            var Q0;
            {var subQ0=sQuery(id+"F0.wireOp",EDGE,"E0.top");var subQ1=sQuery(id+"F12.wireOp",EDGE,"E10.0");var subQ2=sQuery(id+"F12.wireOp",EDGE,"E10.3");Q0=makeQuery(id+"F13.boolean.opBoolean","COPY",EDGE,{"disambiguationData":[TD([makeQuery(id+"F1.opExtrude","SWEPT_FACE",FACE,{"disambiguationData":[OSD([subQ0])]})])],"derivedFrom":makeQuery(id+"F13.opExtrude","SWEPT_EDGE",EDGE,{"disambiguationData":[OSD([subQ1,subQ2])]})});}
            var Q1;
            {var subQ0=sQuery(id+"F0.wireOp",EDGE,"E0.top");var subQ1=sQuery(id+"F12.wireOp",EDGE,"E10.0");var subQ2=sQuery(id+"F12.wireOp",EDGE,"E10.1");Q1=makeQuery(id+"F13.boolean.opBoolean","COPY",EDGE,{"disambiguationData":[TD([makeQuery(id+"F1.opExtrude","SWEPT_FACE",FACE,{"disambiguationData":[OSD([subQ0])]})])],"derivedFrom":makeQuery(id+"F13.opExtrude","SWEPT_EDGE",EDGE,{"disambiguationData":[OSD([subQ1,subQ2])]})});}
            var Q2;
            {var subQ0=sQuery(id+"F0.wireOp",EDGE,"E0.top");var subQ1=sQuery(id+"F12.wireOp",EDGE,"E10.2");var subQ2=sQuery(id+"F12.wireOp",EDGE,"E10.1");Q2=makeQuery(id+"F13.boolean.opBoolean","COPY",EDGE,{"disambiguationData":[TD([makeQuery(id+"F1.opExtrude","SWEPT_FACE",FACE,{"disambiguationData":[OSD([subQ0])]})])],"derivedFrom":makeQuery(id+"F13.opExtrude","SWEPT_EDGE",EDGE,{"disambiguationData":[OSD([subQ2,subQ1])]})});}
            var Q3;
            {var subQ0=sQuery(id+"F0.wireOp",EDGE,"E0.top");var subQ1=sQuery(id+"F12.wireOp",EDGE,"E10.2");var subQ2=sQuery(id+"F12.wireOp",EDGE,"E10.3");Q3=makeQuery(id+"F13.boolean.opBoolean","COPY",EDGE,{"disambiguationData":[TD([makeQuery(id+"F1.opExtrude","SWEPT_FACE",FACE,{"disambiguationData":[OSD([subQ0])]})])],"derivedFrom":makeQuery(id+"F13.opExtrude","SWEPT_EDGE",EDGE,{"disambiguationData":[OSD([subQ1,subQ2])]})});}
            var Q4;
            {var subQ0=sQuery(id+"F0.wireOp",EDGE,"E0.bottom");var subQ1=sQuery(id+"F12.wireOp",EDGE,"E10.1");var subQ2=sQuery(id+"F12.wireOp",EDGE,"E10.2");Q4=makeQuery(id+"F13.boolean.opBoolean","COPY",EDGE,{"disambiguationData":[TD([makeQuery(id+"F1.opExtrude","SWEPT_FACE",FACE,{"disambiguationData":[OSD([subQ0])]})])],"derivedFrom":makeQuery(id+"F13.opExtrude","SWEPT_EDGE",EDGE,{"disambiguationData":[OSD([subQ1,subQ2])]})});}
            var Q5;
            {var subQ0=sQuery(id+"F0.wireOp",EDGE,"E0.bottom");var subQ1=sQuery(id+"F12.wireOp",EDGE,"E10.0");var subQ2=sQuery(id+"F12.wireOp",EDGE,"E10.1");Q5=makeQuery(id+"F13.boolean.opBoolean","COPY",EDGE,{"disambiguationData":[TD([makeQuery(id+"F1.opExtrude","SWEPT_FACE",FACE,{"disambiguationData":[OSD([subQ0])]})])],"derivedFrom":makeQuery(id+"F13.opExtrude","SWEPT_EDGE",EDGE,{"disambiguationData":[OSD([subQ1,subQ2])]})});}
            var Q6;
            {var subQ0=sQuery(id+"F0.wireOp",EDGE,"E0.bottom");var subQ1=sQuery(id+"F12.wireOp",EDGE,"E10.0");var subQ2=sQuery(id+"F12.wireOp",EDGE,"E10.3");Q6=makeQuery(id+"F13.boolean.opBoolean","COPY",EDGE,{"disambiguationData":[TD([makeQuery(id+"F1.opExtrude","SWEPT_FACE",FACE,{"disambiguationData":[OSD([subQ0])]})])],"derivedFrom":makeQuery(id+"F13.opExtrude","SWEPT_EDGE",EDGE,{"disambiguationData":[OSD([subQ1,subQ2])]})});}
            var Q7;
            {var subQ0=sQuery(id+"F0.wireOp",EDGE,"E0.bottom");var subQ1=sQuery(id+"F12.wireOp",EDGE,"E10.2");var subQ2=sQuery(id+"F12.wireOp",EDGE,"E10.3");Q7=makeQuery(id+"F13.boolean.opBoolean","COPY",EDGE,{"disambiguationData":[TD([makeQuery(id+"F1.opExtrude","SWEPT_FACE",FACE,{"disambiguationData":[OSD([subQ0])]})])],"derivedFrom":makeQuery(id+"F13.opExtrude","SWEPT_EDGE",EDGE,{"disambiguationData":[OSD([subQ1,subQ2])]})});}
            fillet(context, id + "F26", {"entities" : qUnion([Q0, Q1, Q2, Q3, Q4, Q5, Q6, Q7]), "radius" : 0.38 * mm, "tangentPropagation" : true, "allowEdgeOverflow" : false});
        }
        {
            var Q0;
            Q0=makeQuery(id+"F13.boolean.opBoolean","INTERSECT",EDGE,{"derivedFrom":[makeQuery(id+"F1.opExtrude","SWEPT_FACE",FACE,{"disambiguationData":[OSD([sQuery(id+"F0.wireOp",EDGE,"E0.top")])]}),makeQuery(id+"F13.opExtrude","SWEPT_FACE",FACE,{"disambiguationData":[OSD([sQuery(id+"F12.wireOp",EDGE,"E10.3")])]})]});
            var Q1;
            Q1=makeQuery(id+"F13.boolean.opBoolean","INTERSECT",EDGE,{"derivedFrom":[makeQuery(id+"F1.opExtrude","SWEPT_FACE",FACE,{"disambiguationData":[OSD([sQuery(id+"F0.wireOp",EDGE,"E0.bottom")])]}),makeQuery(id+"F13.opExtrude","SWEPT_FACE",FACE,{"disambiguationData":[OSD([sQuery(id+"F12.wireOp",EDGE,"E10.3")])]})]});
            chamfer(context, id + "F27", {"entities" : qUnion([Q0, Q1]), "width" : 1.02 * mm, "tangentPropagation" : true});
        }
        {
            var Q0;
            Q0=qCreatedBy(makeId("Front.planeOp"),FACE);
            var sketch = newSketch(context, id + "F28", { "sketchPlane" : qUnion([Q0])});
            skLineSegment(sketch, "E34.bottom", {"start": v(-8.62, 15.11) * mm, "end": v(-12.43, 15.11) * mm});
            skLineSegment(sketch, "E34.top", {"start": v(-8.62, 6.22) * mm, "end": v(-12.43, 6.22) * mm});
            skLineSegment(sketch, "E34.left", {"start": v(-8.62, 15.11) * mm, "end": v(-8.62, 6.22) * mm});
            skLineSegment(sketch, "E34.right", {"start": v(-12.43, 15.11) * mm, "end": v(-12.43, 6.22) * mm});
            skSolve(sketch);
        }
        {
            var Q0;
            Q0 = qSketchRegion(id + "F28", true);
            extrude(context, id + "F29", {"entities" : qUnion([Q0]), "operationType" : NewBodyOperationType.REMOVE, "endBound" : BoundingType.THROUGH_ALL, "oppositeDirection" : true, "depth" : 25.4 * mm, "offsetDistance" : 25.4 * mm});
        }
        {
            var Q0;
            Q0=makeQuery(id+"F29.boolean.opBoolean","COPY",EDGE,{"derivedFrom":makeQuery(id+"F29.opExtrude","SWEPT_EDGE",EDGE,{"disambiguationData":[OSD([sQuery(id+"F28.wireOp",EDGE,"E34.top"),sQuery(id+"F28.wireOp",EDGE,"E34.right")])]})});
            var Q1;
            Q1=makeQuery(id+"F29.boolean.opBoolean","COPY",EDGE,{"derivedFrom":makeQuery(id+"F29.opExtrude","SWEPT_EDGE",EDGE,{"disambiguationData":[OSD([sQuery(id+"F28.wireOp",EDGE,"E34.top"),sQuery(id+"F28.wireOp",EDGE,"E34.left")])]})});
            var Q2;
            Q2=makeQuery(id+"F29.boolean.opBoolean","COPY",EDGE,{"derivedFrom":makeQuery(id+"F29.opExtrude","SWEPT_EDGE",EDGE,{"disambiguationData":[OSD([sQuery(id+"F28.wireOp",EDGE,"E34.bottom"),sQuery(id+"F28.wireOp",EDGE,"E34.left")])]})});
            var Q3;
            Q3=makeQuery(id+"F29.boolean.opBoolean","COPY",EDGE,{"derivedFrom":makeQuery(id+"F29.opExtrude","SWEPT_EDGE",EDGE,{"disambiguationData":[OSD([sQuery(id+"F28.wireOp",EDGE,"E34.bottom"),sQuery(id+"F28.wireOp",EDGE,"E34.right")])]})});
            fillet(context, id + "F30", {"entities" : qUnion([Q0, Q1, Q2, Q3]), "radius" : 0.38 * mm, "tangentPropagation" : true, "allowEdgeOverflow" : false});
        }
        {
            var Q0;
            Q0=makeQuery(id+"F29.boolean.opBoolean","INTERSECT",EDGE,{"derivedFrom":[makeQuery(id+"F1.opExtrude","SWEPT_FACE",FACE,{"disambiguationData":[OSD([sQuery(id+"F0.wireOp",EDGE,"E0.bottom")])]}),makeQuery(id+"F29.opExtrude","SWEPT_FACE",FACE,{"disambiguationData":[OSD([sQuery(id+"F28.wireOp",EDGE,"E34.right")])]})]});
            chamfer(context, id + "F31", {"entities" : qUnion([Q0]), "width" : 0.64 * mm, "tangentPropagation" : true});
        }
        {
            var Q0;
            Q0=qCreatedBy(makeId("Front.planeOp"),FACE);
            var sketch = newSketch(context, id + "F32", { "sketchPlane" : qUnion([Q0])});
            skLineSegment(sketch, "E35.0", {"start": v(-6.86, 3.68) * mm, "end": v(-6.86, 17.02) * mm, "construction": true});
            skPoint(sketch, "E36", {"position": v(-6.86, 10.35) * mm});
            skCircle(sketch, "E37", {"center": v(-10.92, 10.35) * mm, "radius": 1.02 * mm});
            skSolve(sketch);
        }
        {
            var Q0;
            Q0 = qSketchRegion(id + "F32", true);
            extrude(context, id + "F33", {"entities" : qUnion([Q0]), "operationType" : NewBodyOperationType.REMOVE, "endBound" : BoundingType.THROUGH_ALL, "depth" : 25.4 * mm, "offsetDistance" : 25.4 * mm});
        }
        {
            var Q0;
            Q0=makeQuery(id+"F33.boolean.opBoolean","INTERSECT",EDGE,{"derivedFrom":[makeQuery(id+"F1.opExtrude","SWEPT_FACE",FACE,{"disambiguationData":[OSD([sQuery(id+"F0.wireOp",EDGE,"E0.top")])]}),makeQuery(id+"F33.opExtrude","SWEPT_FACE",FACE,{"disambiguationData":[OSD([sQuery(id+"F32.wireOp",EDGE,"E37")])]})]});
            chamfer(context, id + "F34", {"entities" : qUnion([Q0]), "width" : 0.38 * mm, "tangentPropagation" : true});
        }
        {
            var Q0;
            Q0=makeQuery(id+"F3.opShell","OFFSET_FACE",FACE,{"disambiguationData":[OSD([sQuery(id+"F0.wireOp",EDGE,"E0.top")])]});
            var sketch = newSketch(context, id + "F35", { "sketchPlane" : qUnion([Q0])});
            skCircle(sketch, "E38.0", {"center": v(10.92, 10.35) * mm, "radius": 0.89 * mm});
            skSolve(sketch);
        }
        {
            var Q0;
            Q0 = qSketchRegion(id + "F35", true);
            extrude(context, id + "F36", {"entities" : qUnion([Q0]), "oppositeDirection" : true, "depth" : 0.5 * mm, "offsetDistance" : 25.4 * mm});
        }
        {
            var Q0;
            Q0=makeQuery(id+"F11.boolean.opBoolean","COPY",FACE,{"derivedFrom":makeQuery(id+"F11.opExtrude","CAP_FACE",FACE,{"disambiguationData":[OSD([sQuery(id+"F7.wireOp",EDGE,"E2.0"),sQuery(id+"F7.wireOp",EDGE,"E2.1"),sQuery(id+"F7.wireOp",EDGE,"E2.2"),sQuery(id+"F7.wireOp",EDGE,"E2.3"),sQuery(id+"F7.wireOp",EDGE,"E2.4"),sQuery(id+"F7.wireOp",EDGE,"E2.5"),sQuery(id+"F7.wireOp",EDGE,"E2.6"),sQuery(id+"F7.wireOp",EDGE,"E2.7")])],"isStart":false})});
            var sketch = newSketch(context, id + "F37", { "sketchPlane" : qUnion([Q0])});
            skText(sketch, "E39", { "text": "sicuro", "fontName": "OpenSans-Regular.ttf"});
            skPoint(sketch, "E40", {"position": v(0, -8.52) * mm});
            const initialGuessF37  = {"E39": [0.00216, -0.00852, 0, 1, 0.00432]};
            skSetInitialGuess(sketch, initialGuessF37);
            skSolve(sketch);
        }
        {
            var Q0;
            Q0 = qSketchRegion(id + "F37", true);
            var Q1;
            Q1 = qBodyType(qCreatedBy(id + "F37" ,EDGE), BodyType.WIRE);
            var Q2;
            Q2 = qBodyType(qCreatedBy(id + "F37" ,EDGE), BodyType.WIRE);
            extrude(context, id + "F38", {"entities" : qUnion([Q0]), "operationType" : NewBodyOperationType.REMOVE, "surfaceEntities" : qUnion([Q1, Q2]), "oppositeDirection" : true, "depth" : 0.08 * mm, "offsetDistance" : 25.4 * mm});
        }
        {
            var Q0;
            Q0=makeQuery(id+"F20.opExtrude","CAP_EDGE",EDGE,{"disambiguationData":[OSD([sQuery(id+"F19.wireOp",EDGE,"E24.7")])],"isStart":true});
            var Q1;
            Q1=makeQuery(id+"F20.opExtrude","CAP_EDGE",EDGE,{"disambiguationData":[OSD([sQuery(id+"F19.wireOp",EDGE,"E25.7")])],"isStart":true});
            chamfer(context, id + "F39", {"entities" : qUnion([Q0, Q1]), "width" : 0.5 * mm, "tangentPropagation" : true});
        }
        {
            var Q0;
            Q0=makeQuery(id+"F20.opExtrude","CAP_FACE",FACE,{"disambiguationData":[OSD([sQuery(id+"F19.wireOp",EDGE,"E24.0"),sQuery(id+"F19.wireOp",EDGE,"E24.1"),sQuery(id+"F19.wireOp",EDGE,"E24.2"),sQuery(id+"F19.wireOp",EDGE,"E24.3"),sQuery(id+"F19.wireOp",EDGE,"E24.4"),sQuery(id+"F19.wireOp",EDGE,"E24.5"),sQuery(id+"F19.wireOp",EDGE,"E24.6"),sQuery(id+"F19.wireOp",EDGE,"E24.7")])],"isStart":true});
            var sketch = newSketch(context, id + "F40", { "sketchPlane" : qUnion([Q0])});
            skPoint(sketch, "E41", {"position": v(-4.28, -17.3) * mm});
            skPoint(sketch, "E42", {"position": v(-4.32, -17.78) * mm});
            skPoint(sketch, "E43", {"position": v(0, -22.1) * mm});
            skLineSegment(sketch, "E44", {"start": v(-4.32, -17.78) * mm, "end": v(3.31, -17.78) * mm, "construction": true});
            skLineSegment(sketch, "E45", {"start": v(0, -22.1) * mm, "end": v(0, -17.78) * mm, "construction": true});
            skArc(sketch, "E46", {"start": v(-2, -18.1) * mm, "mid": v(-2, -18.1) * mm, "end": v(-2, -18.1) * mm});
            skArc(sketch, "E47", {"start": v(-0.99, -18.77) * mm, "mid": v(1.4, -17.78) * mm, "end": v(-0.99, -16.8) * mm});
            skArc(sketch, "E48", {"start": v(0, -18.1) * mm, "mid": v(0.32, -17.78) * mm, "end": v(0, -17.46) * mm});
            skArc(sketch, "E49", {"start": v(-2, -17.46) * mm, "mid": v(-2.35, -17.78) * mm, "end": v(-2, -18.1) * mm});
            skLineSegment(sketch, "E50", {"start": v(-2.03, -18.1) * mm, "end": v(0, -18.1) * mm});
            skLineSegment(sketch, "E51", {"start": v(0, -17.46) * mm, "end": v(-2.03, -17.46) * mm});
            skLineSegment(sketch, "E52", {"start": v(-1.57, -18.73) * mm, "end": v(-1.08, -18.73) * mm});
            skLineSegment(sketch, "E53", {"start": v(-1.57, -16.83) * mm, "end": v(-1.08, -16.83) * mm});
            skArc(sketch, "E54.trimOffspring", {"start": v(-1.67, -18.93) * mm, "mid": v(2.03, -17.78) * mm, "end": v(-1.67, -16.63) * mm});
            skArc(sketch, "E55.trimOffspring", {"start": v(-2, -17.46) * mm, "mid": v(-2, -17.46) * mm, "end": v(-2, -17.46) * mm});
            skPoint(sketch, "E56.visualSharp", {"position": v(-1.8, -18.73) * mm});
            skArc(sketch, "E56.filletArc", {"start": v(-1.57, -18.73) * mm, "mid": v(-1.68, -18.8) * mm, "end": v(-1.67, -18.93) * mm});
            skPoint(sketch, "E57.visualSharp", {"position": v(-1.02, -18.73) * mm});
            skArc(sketch, "E57.filletArc", {"start": v(-0.99, -18.77) * mm, "mid": v(-1.03, -18.74) * mm, "end": v(-1.08, -18.73) * mm});
            skPoint(sketch, "E58.visualSharp", {"position": v(-1.02, -16.83) * mm});
            skArc(sketch, "E58.filletArc", {"start": v(-1.08, -16.83) * mm, "mid": v(-1.03, -16.82) * mm, "end": v(-0.99, -16.8) * mm});
            skPoint(sketch, "E59.visualSharp", {"position": v(-1.8, -16.83) * mm});
            skArc(sketch, "E59.filletArc", {"start": v(-1.67, -16.63) * mm, "mid": v(-1.68, -16.76) * mm, "end": v(-1.57, -16.83) * mm});
            skSolve(sketch);
        }
        {
            var Q0;
            Q0 = qSketchRegion(id + "F40", true);
            extrude(context, id + "F41", {"entities" : qUnion([Q0]), "operationType" : NewBodyOperationType.REMOVE, "oppositeDirection" : true, "depth" : 0.25 * mm, "offsetDistance" : 25.4 * mm});
        }
        {
            var Q0;
            Q0=makeQuery(id+"F20.opExtrude","CAP_FACE",FACE,{"disambiguationData":[OSD([sQuery(id+"F19.wireOp",EDGE,"E25.0"),sQuery(id+"F19.wireOp",EDGE,"E25.1"),sQuery(id+"F19.wireOp",EDGE,"E25.2"),sQuery(id+"F19.wireOp",EDGE,"E25.3"),sQuery(id+"F19.wireOp",EDGE,"E25.4"),sQuery(id+"F19.wireOp",EDGE,"E25.5"),sQuery(id+"F19.wireOp",EDGE,"E25.6"),sQuery(id+"F19.wireOp",EDGE,"E25.7")])],"isStart":true});
            var sketch = newSketch(context, id + "F42", { "sketchPlane" : qUnion([Q0])});
            skLineSegment(sketch, "E60.0", {"start": v(-4.32, 20.32) * mm, "end": v(-4.32, 15.24) * mm, "construction": true});
            skLineSegment(sketch, "E61.0", {"start": v(-2.54, 13.46) * mm, "end": v(2.54, 13.46) * mm, "construction": true});
            skPoint(sketch, "E62", {"position": v(-4.32, 17.78) * mm});
            skPoint(sketch, "E63", {"position": v(0, 13.46) * mm});
            skLineSegment(sketch, "E64", {"start": v(0, 13.46) * mm, "end": v(0, 19.74) * mm, "construction": true});
            skLineSegment(sketch, "E65", {"start": v(-4.32, 17.78) * mm, "end": v(0, 17.78) * mm, "construction": true});
            skLineSegment(sketch, "E66.bottom", {"start": v(2.54, 19.81) * mm, "end": v(-0.25, 19.81) * mm});
            skLineSegment(sketch, "E66.top", {"start": v(2.54, 15.75) * mm, "end": v(-0.25, 15.75) * mm});
            skLineSegment(sketch, "E66.left", {"start": v(2.54, 19.81) * mm, "end": v(2.54, 15.75) * mm});
            skLineSegment(sketch, "E66.right", {"start": v(-0.25, 19.81) * mm, "end": v(-0.25, 19.43) * mm});
            skPoint(sketch, "E66.middle", {"position": v(1.14, 17.78) * mm});
            skArc(sketch, "E67", {"start": v(-0.89, 19.43) * mm, "mid": v(-2.54, 17.78) * mm, "end": v(-0.89, 16.13) * mm});
            skArc(sketch, "E68", {"start": v(-0.89, 18.8) * mm, "mid": v(-1.9, 17.78) * mm, "end": v(-0.89, 16.76) * mm});
            skLineSegment(sketch, "E69", {"start": v(-0.89, 16.13) * mm, "end": v(-0.25, 16.13) * mm});
            skLineSegment(sketch, "E70", {"start": v(-0.89, 16.76) * mm, "end": v(-0.25, 16.76) * mm});
            skLineSegment(sketch, "E71", {"start": v(-0.89, 18.8) * mm, "end": v(-0.25, 18.8) * mm});
            skLineSegment(sketch, "E72", {"start": v(-0.89, 19.43) * mm, "end": v(-0.25, 19.43) * mm});
            skLineSegment(sketch, "E73.trimOffspring", {"start": v(-0.25, 16.13) * mm, "end": v(-0.25, 15.75) * mm});
            skLineSegment(sketch, "E74.trimOffspring", {"start": v(-0.25, 18.8) * mm, "end": v(-0.25, 16.76) * mm});
            skSolve(sketch);
        }
        {
            var Q0;
            Q0 = qSketchRegion(id + "F42", true);
            extrude(context, id + "F43", {"entities" : qUnion([Q0]), "operationType" : NewBodyOperationType.REMOVE, "oppositeDirection" : true, "depth" : 0.25 * mm, "offsetDistance" : 25.4 * mm});
        }
    });
